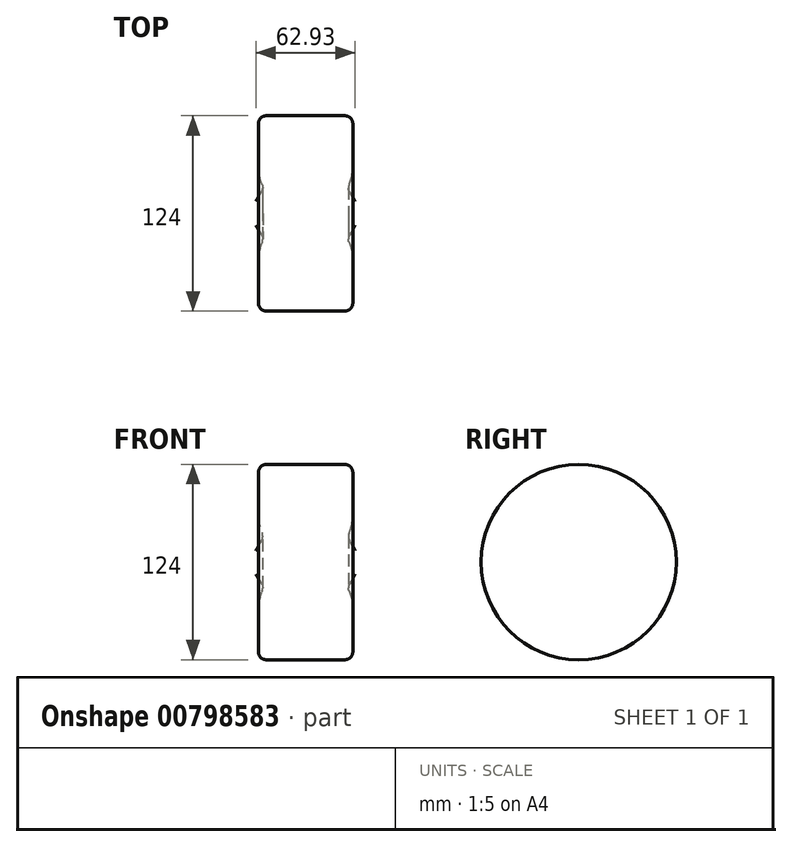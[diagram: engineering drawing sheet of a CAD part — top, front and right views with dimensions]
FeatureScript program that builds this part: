
annotation { "Feature Type Name" : "Feature", "Feature Type Description" : "" }
export const myFeature = defineFeature(function(context is Context, id is Id, definition is map)
    precondition{}
    {
        {
            var Q0;
            Q0=qCreatedBy(makeId("Front.planeOp"),FACE);
            var sketch = newSketch(context, id + "F0", { "sketchPlane" : qUnion([Q0])});
            skLineSegment(sketch, "E0.top", {"start": v(-64.72, 0) * mm, "end": v(-14.72, 0) * mm});
            skLineSegment(sketch, "E0.left", {"start": v(-69.72, 32) * mm, "end": v(-69.72, 5) * mm});
            skLineSegment(sketch, "E0.right", {"start": v(-9.72, 32) * mm, "end": v(-9.72, 5) * mm});
            skArc(sketch, "E1", {"start": v(-9.72, 32) * mm, "mid": v(-10.33, 38.02) * mm, "end": v(-12.13, 43.79) * mm});
            skLineSegment(sketch, "E2.0", {"start": v(-66.86, 62) * mm, "end": v(-12.59, 62) * mm});
            skLineSegment(sketch, "E2.1", {"start": v(-8.26, 54.5) * mm, "end": v(-11.87, 48.25) * mm});
            skLineSegment(sketch, "E2.2", {"start": v(-67.58, 48.25) * mm, "end": v(-71.19, 54.5) * mm});
            skPoint(sketch, "E2.0.midPoint", {"position": v(-39.72, 62) * mm});
            skPoint(sketch, "E2.cCircle.center.orphan", {"position": v(-39.72, 41.33) * mm});
            skPoint(sketch, "E3.orphan", {"position": v(-39.72, 0) * mm});
            skArc(sketch, "E4.trimOffspring", {"start": v(-67.31, 43.79) * mm, "mid": v(-69.11, 38.02) * mm, "end": v(-69.72, 32) * mm});
            skPoint(sketch, "E5.visualSharp", {"position": v(-69.72, 0) * mm});
            skArc(sketch, "E5.filletArc", {"start": v(-69.72, 5) * mm, "mid": v(-68.26, 1.46) * mm, "end": v(-64.72, 0) * mm});
            skPoint(sketch, "E6.visualSharp", {"position": v(-9.72, 0) * mm});
            skArc(sketch, "E6.filletArc", {"start": v(-14.72, 0) * mm, "mid": v(-11.19, 1.46) * mm, "end": v(-9.72, 5) * mm});
            skPoint(sketch, "E7.visualSharp", {"position": v(-66.27, 45.98) * mm});
            skArc(sketch, "E7.filletArc", {"start": v(-67.31, 43.79) * mm, "mid": v(-66.92, 46.05) * mm, "end": v(-67.58, 48.25) * mm});
            skPoint(sketch, "E8.visualSharp", {"position": v(-13.18, 45.98) * mm});
            skArc(sketch, "E8.filletArc", {"start": v(-11.87, 48.25) * mm, "mid": v(-12.53, 46.05) * mm, "end": v(-12.13, 43.79) * mm});
            skPoint(sketch, "E9.visualSharp", {"position": v(-3.93, 62) * mm});
            skArc(sketch, "E9.filletArc", {"start": v(-8.26, 54.5) * mm, "mid": v(-8.26, 59.5) * mm, "end": v(-12.59, 62) * mm});
            skPoint(sketch, "E10.visualSharp", {"position": v(-75.52, 62) * mm});
            skArc(sketch, "E10.filletArc", {"start": v(-66.86, 62) * mm, "mid": v(-71.19, 59.5) * mm, "end": v(-71.19, 54.5) * mm});
            skSolve(sketch);
        }
        {
            var Q0;
            Q0=makeQuery(id+"F0.imprint","IMPRINT",FACE,{"disambiguationData":[TD([[makeQuery(id+"F0.imprint","IMPRINT",EDGE,{"derivedFrom":sQuery(id+"F0.wireOp",EDGE,"E0.top")}),1.0]])]});
            var Q1;
            Q1=sQuery(id+"F0.wireOp",EDGE,"E2.0");
            revolve(context, id + "F1", {"surfaceOperationType" : NewSurfaceOperationType.NEW, "entities" : qUnion([Q0]), "axis" : qUnion([Q1]), "revolveType" : RevolveType.SYMMETRIC, "angle" : 360 * degree});
        }
    });
